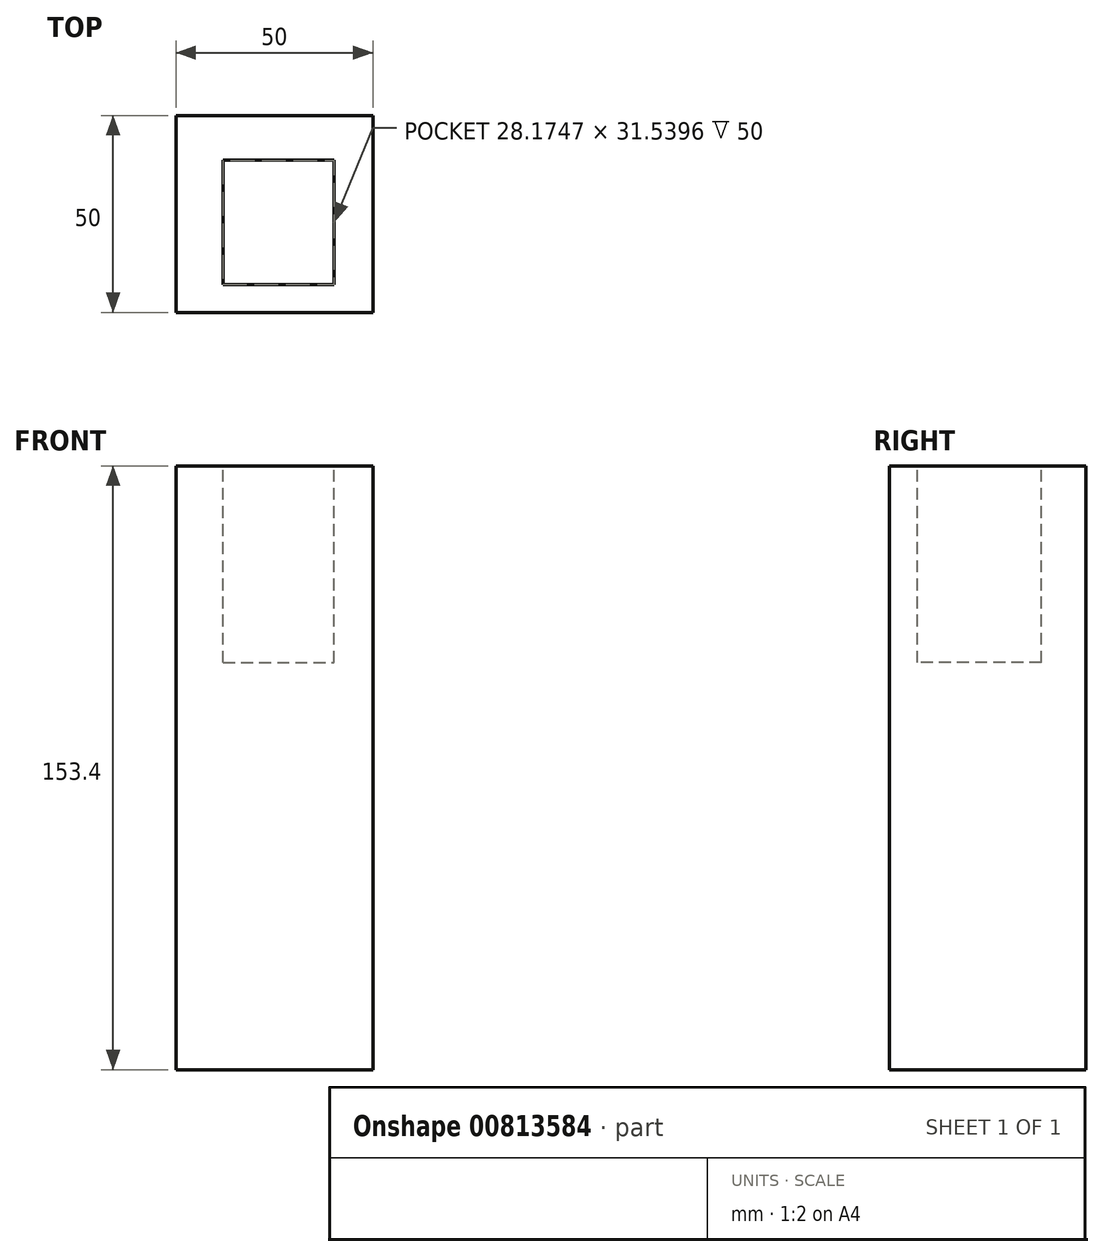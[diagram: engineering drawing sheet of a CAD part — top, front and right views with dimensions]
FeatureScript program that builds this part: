
annotation { "Feature Type Name" : "Feature", "Feature Type Description" : "" }
export const myFeature = defineFeature(function(context is Context, id is Id, definition is map)
    precondition{}
    {
        {
            var Q0;
            Q0=qCreatedBy(makeId("Top.planeOp"),FACE);
            var sketch = newSketch(context, id + "F0", { "sketchPlane" : qUnion([Q0])});
            skLineSegment(sketch, "E0.bottom", {"start": v(-17.13, 21.84) * mm, "end": v(32.87, 21.84) * mm});
            skLineSegment(sketch, "E0.top", {"start": v(-17.13, -28.16) * mm, "end": v(32.87, -28.16) * mm});
            skLineSegment(sketch, "E0.left", {"start": v(-17.13, 21.84) * mm, "end": v(-17.13, -28.16) * mm});
            skLineSegment(sketch, "E0.right", {"start": v(32.87, 21.84) * mm, "end": v(32.87, -28.16) * mm});
            skSolve(sketch);
        }
        {
            var Q0;
            Q0 = qSketchRegion(id + "F0", true);
            extrude(context, id + "F1", {"entities" : qUnion([Q0]), "flatOperationType" : FlatOperationType.REMOVE, "depth" : 153.4 * mm, "offsetDistance" : 25 * mm, "domain" : OperationDomain.MODEL});
        }
        {
            var Q0;
            Q0=makeQuery(id+"F1.opExtrude","CAP_FACE",FACE,{"disambiguationData":[OSD([sQuery(id+"F0.wireOp",EDGE,"E0.bottom"),sQuery(id+"F0.wireOp",EDGE,"E0.top"),sQuery(id+"F0.wireOp",EDGE,"E0.left"),sQuery(id+"F0.wireOp",EDGE,"E0.right")])],"isStart":false});
            var sketch = newSketch(context, id + "F2", { "sketchPlane" : qUnion([Q0])});
            skLineSegment(sketch, "E1.bottom", {"start": v(-5.2, 10.47) * mm, "end": v(22.98, 10.47) * mm});
            skLineSegment(sketch, "E1.top", {"start": v(-5.2, -21.07) * mm, "end": v(22.98, -21.07) * mm});
            skLineSegment(sketch, "E1.left", {"start": v(-5.2, 10.47) * mm, "end": v(-5.2, -21.07) * mm});
            skLineSegment(sketch, "E1.right", {"start": v(22.98, 10.47) * mm, "end": v(22.98, -21.07) * mm});
            skSolve(sketch);
        }
        {
            var Q0;
            Q0 = qSketchRegion(id + "F2", true);
            extrude(context, id + "F3", {"entities" : qUnion([Q0]), "operationType" : NewBodyOperationType.REMOVE, "oppositeDirection" : true, "depth" : 50 * mm, "offsetDistance" : 25 * mm});
        }
    });
